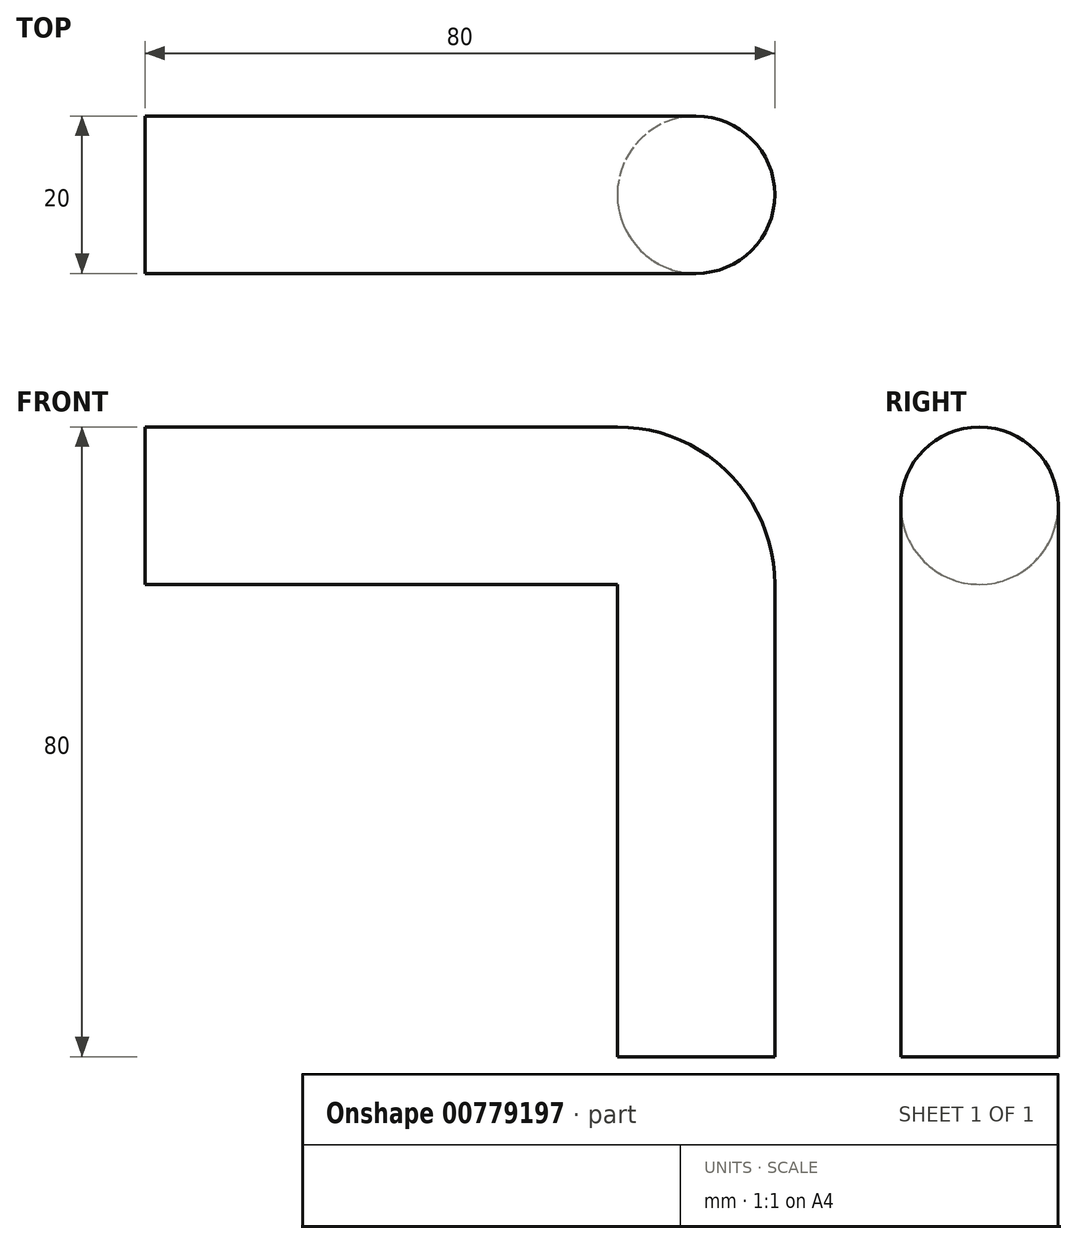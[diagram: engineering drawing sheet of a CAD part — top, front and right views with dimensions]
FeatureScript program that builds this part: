
annotation { "Feature Type Name" : "Feature", "Feature Type Description" : "" }
export const myFeature = defineFeature(function(context is Context, id is Id, definition is map)
    precondition{}
    {
        {
            var Q0;
            Q0=qCreatedBy(makeId("Top.planeOp"),FACE);
            var sketch = newSketch(context, id + "F0", { "sketchPlane" : qUnion([Q0])});
            skCircle(sketch, "E0", {"center": v(0, 0) * mm, "radius": 10 * mm});
            skSolve(sketch);
        }
        {
            var Q0;
            Q0=qCreatedBy(makeId("Front.planeOp"),FACE);
            var sketch = newSketch(context, id + "F1", { "sketchPlane" : qUnion([Q0])});
            skLineSegment(sketch, "E1", {"start": v(0, 0) * mm, "end": v(0, 60) * mm});
            skLineSegment(sketch, "E2", {"start": v(-10, 70) * mm, "end": v(-70, 70) * mm});
            skPoint(sketch, "E3.visualSharp", {"position": v(0, 70) * mm});
            skArc(sketch, "E3.filletArc", {"start": v(0, 60) * mm, "mid": v(-2.93, 67.07) * mm, "end": v(-10, 70) * mm});
            skSolve(sketch);
        }
        {
            var Q0;
            Q0=makeQuery(id+"F0.imprint","IMPRINT",FACE,{"disambiguationData":[TD([[makeQuery(id+"F0.imprint","IMPRINT",EDGE,{"derivedFrom":sQuery(id+"F0.wireOp",EDGE,"E0")}),1.0]])]});
            var Q1;
            Q1=sQuery(id+"F1.wireOp",EDGE,"E2");
            var Q2;
            Q2=sQuery(id+"F1.wireOp",EDGE,"E3.filletArc");
            var Q3;
            Q3=sQuery(id+"F1.wireOp",EDGE,"E1");
            sweep(context, id + "F2", {"profiles" : qUnion([Q0]), "path" : qUnion([Q1, Q2, Q3])});
        }
    });
